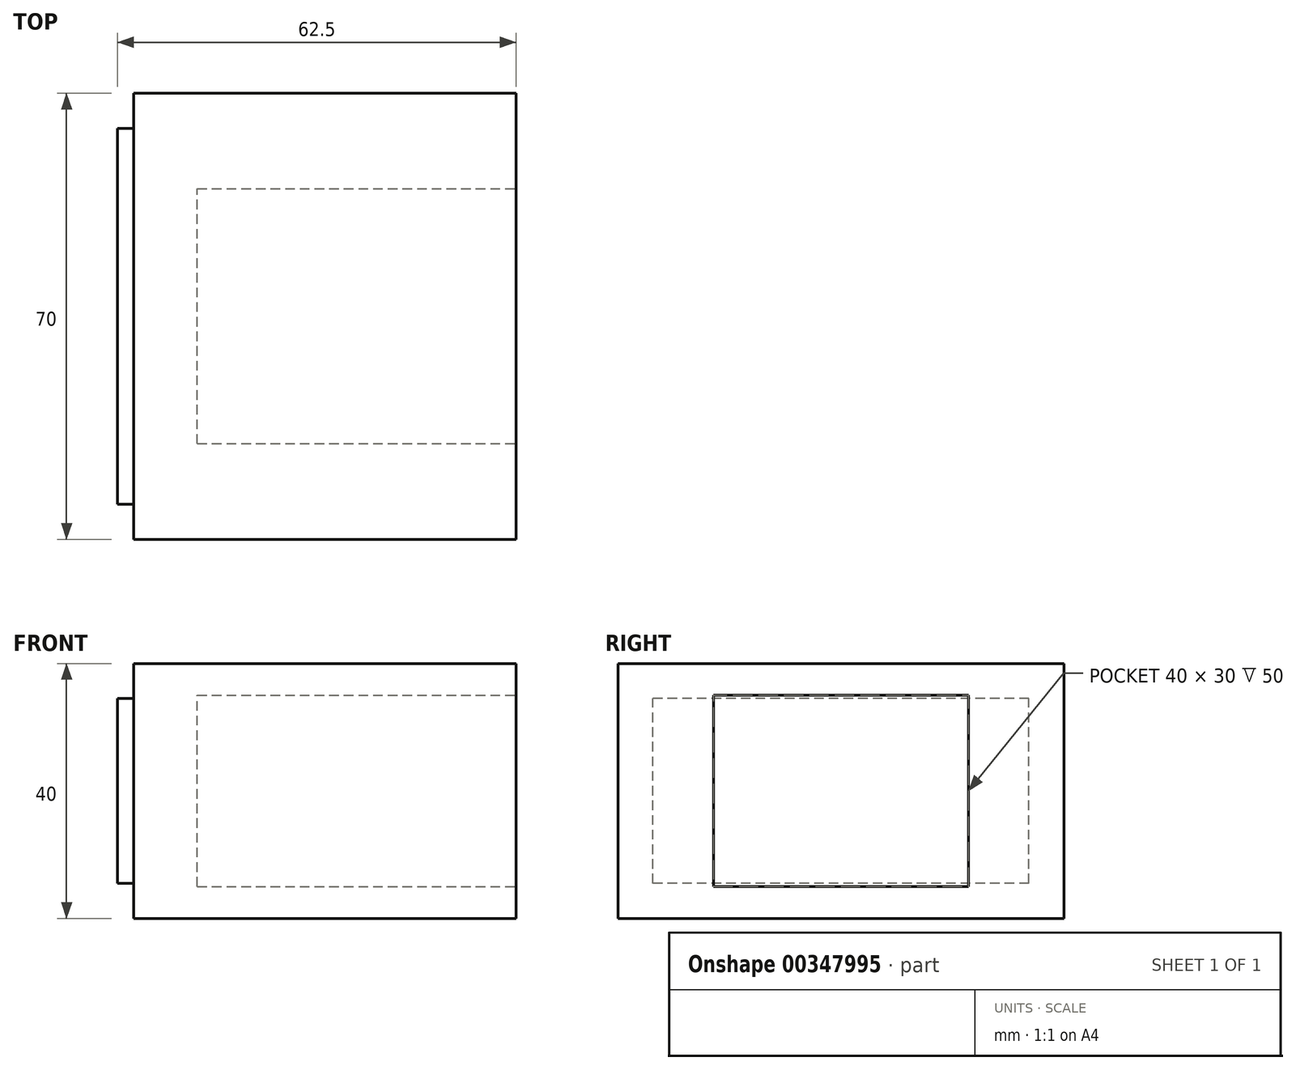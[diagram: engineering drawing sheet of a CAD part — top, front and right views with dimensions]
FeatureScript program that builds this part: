
annotation { "Feature Type Name" : "Feature", "Feature Type Description" : "" }
export const myFeature = defineFeature(function(context is Context, id is Id, definition is map)
    precondition{}
    {
        {
            var Q0;
            Q0=qCreatedBy(makeId("Right.planeOp"),FACE);
            var sketch = newSketch(context, id + "F0", { "sketchPlane" : qUnion([Q0])});
            skLineSegment(sketch, "E0.bottom", {"start": v(0, 0) * mm, "end": v(70, 0) * mm});
            skLineSegment(sketch, "E0.top", {"start": v(0, 40) * mm, "end": v(70, 40) * mm});
            skLineSegment(sketch, "E0.left", {"start": v(0, 0) * mm, "end": v(0, 40) * mm});
            skLineSegment(sketch, "E0.right", {"start": v(70, 0) * mm, "end": v(70, 40) * mm});
            skSolve(sketch);
        }
        {
            var Q0;
            Q0=qSketchRegion(id+"F0",true);
            extrude(context, id + "F1", {"entities" : qUnion([Q0]), "depth" : 60 * mm});
        }
        {
            var Q0;
            Q0=makeQuery(id+"F1.opExtrude","CAP_FACE",FACE,{"disambiguationData":[OSD([sQuery(id+"F0.wireOp",EDGE,"E0.bottom"),sQuery(id+"F0.wireOp",EDGE,"E0.top"),sQuery(id+"F0.wireOp",EDGE,"E0.left"),sQuery(id+"F0.wireOp",EDGE,"E0.right")])],"isStart":false});
            var sketch = newSketch(context, id + "F2", { "sketchPlane" : qUnion([Q0])});
            skLineSegment(sketch, "E1.bottom", {"start": v(15, 5) * mm, "end": v(55, 5) * mm});
            skLineSegment(sketch, "E1.top", {"start": v(15, 35) * mm, "end": v(55, 35) * mm});
            skLineSegment(sketch, "E1.left", {"start": v(15, 5) * mm, "end": v(15, 35) * mm});
            skLineSegment(sketch, "E1.right", {"start": v(55, 5) * mm, "end": v(55, 35) * mm});
            skSolve(sketch);
        }
        {
            var Q0;
            Q0=qSketchRegion(id+"F2",true);
            extrude(context, id + "F3", {"entities" : qUnion([Q0]), "operationType" : NewBodyOperationType.REMOVE, "oppositeDirection" : true, "depth" : 50 * mm});
        }
        {
            var Q0;
            Q0=makeQuery(id+"F1.opExtrude","CAP_FACE",FACE,{"disambiguationData":[OSD([sQuery(id+"F0.wireOp",EDGE,"E0.bottom"),sQuery(id+"F0.wireOp",EDGE,"E0.top"),sQuery(id+"F0.wireOp",EDGE,"E0.left"),sQuery(id+"F0.wireOp",EDGE,"E0.right")])],"isStart":true});
            var sketch = newSketch(context, id + "F4", { "sketchPlane" : qUnion([Q0])});
            skLineSegment(sketch, "E2.bottom", {"start": v(-64.5, 5.5) * mm, "end": v(-5.5, 5.5) * mm});
            skLineSegment(sketch, "E2.top", {"start": v(-64.5, 34.5) * mm, "end": v(-5.5, 34.5) * mm});
            skLineSegment(sketch, "E2.left", {"start": v(-64.5, 5.5) * mm, "end": v(-64.5, 34.5) * mm});
            skLineSegment(sketch, "E2.right", {"start": v(-5.5, 5.5) * mm, "end": v(-5.5, 34.5) * mm});
            skSolve(sketch);
        }
        {
            var Q0;
            Q0=qSketchRegion(id+"F4",true);
            extrude(context, id + "F5", {"entities" : qUnion([Q0]), "operationType" : NewBodyOperationType.ADD, "depth" : 2.5 * mm});
        }
    });
